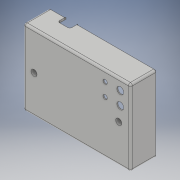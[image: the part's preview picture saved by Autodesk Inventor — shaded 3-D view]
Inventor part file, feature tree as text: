
AUTODESK INVENTOR PART (.ipt)
format: ipt  version: 2019 (Build 230136000, 136)  size: 464,384 bytes
history: native  units: mm
features: other x12, sketch x12, extrude x10, reference x6, fillet x3, projected_geometry x2, shell x1, split x1, hole x1, chamfer x1
ambient origin geometry x8: Origin, YZ Plane, XZ Plane, XY Plane, X Axis, Y Axis, Z Axis, Center Point
bodies: Solid1 (feature_tree)
feature tree (49):
  extrude  "Extrusion1"  Depth=75.0mm
  shell  "Shell1"  Thickness=35.0mm
  fillet  "Fillet2"  Radius=2.0mm
  extrude  "Extrusion10"  Depth=8.0mm
  extrude  "Extrusion11"  Depth=15.0mm
  fillet  "Fillet4"  Radius=15.0mm
  split  "Split1"
  extrude  "Extrusion2"  Depth=5.0mm
  extrude  "Extrusion3"  Depth=3.0mm TaperAngle=0.0deg
  fillet  "Fillet1"  Radius=2.0mm
  other  "Lip1"
  other  "Lip2"
  extrude  "Extrusion4"  Depth=1.0mm
  hole  "Hole1"  [1 undecoded]
  extrude  "Extrusion5"  Depth=8.0mm
  extrude  "Extrusion6"  Depth=23.5mm TaperAngle=0.0deg
  extrude  "Extrusion7"  Depth=5.5mm
  extrude  "Extrusion8"  Depth=3.0mm TaperAngle=0.0deg
  chamfer  "Chamfer1"  Distance=2.0mm
  sketch  "Sketch1"  dims[d0=106.0mm d1=75.0mm d2=35.0mm d3=0.0mm d4=2.0mm]
  sketch  "Sketch2"  dims[d5=9.0mm d6=8.0mm]
  sketch  "Sketch3"  dims[d7=5.0mm d8=0.0mm d9=15.0mm d10=15.0mm]
  reference  "Reference1"
  reference  "Reference2"
  reference  "Reference3"
  reference  "Reference4"
  sketch  "Sketch4"  dims[d11=5.0mm d12=5.0mm]
  projected_geometry  "Projected Loop1"
  sketch  "Sketch5"  dims[d13=4.0mm d14=3.0mm d15=0.0mm d16=2.0mm]
  sketch  "Sketch6"  dims[d17=2.0mm]
  sketch  "Sketch7"  dims[d18=1.0mm d19=1.0mm d20=0.0mm d21=0.0mm d22=0.0mm d23=0.0mm]
  projected_geometry  "Projected Loop2"
  sketch  "Sketch8"  dims[d24=1.0mm d25=1.0mm d26=0.0mm d27=0.0mm d28=0.0mm d29=0.0mm d30=2.6mm]
  sketch  "Sketch9"  dims[d31=2.6mm d32=2.6mm]
  sketch  "Sketch10"  dims[d33=2.6mm d34=8.0mm d35=2.6mm]
  reference  "Reference5"
  reference  "Reference6"
  sketch  "Sketch12"  dims[d36=8.0mm d37=2.6mm]
  sketch  "Sketch13"  dims[d38=3.3mm d39=6.0mm d40=6.0mm d41=21.5mm d42=90.0deg d43=36.25mm d44=0.0mm d45=23.5mm d46=0.0mm d47=5.5mm d48=3.0mm d49=0.0mm d50=2.0mm d51=6.8mm d52=10.0mm d53=10.0mm d54=13.0mm d55=4.3mm d56=15.0mm d57=3.0mm d58=0.0mm d59=11.0mm d60=6.0mm d61=1.0mm d62=0.0mm d63=11.0mm d64=11.0mm d65=30.0mm d66=28.0mm d67=5.1mm d68=0.0mm d69=7.0mm d74=16.0mm d75=12.0mm d76=17.0mm d77=8.0mm d78=10.0mm d79=0.0mm d81=8.0mm d82=17.0mm d83=29.0mm d84=30.0mm d85=10.0mm d86=0.0mm d87=2.0mm d88=8.0mm d89=12.0mm d90=24.375mm d91=18.504mm d92=1.0mm d93=3.5mm d94=2.0mm d95=45.0deg]
  other  "Top"
  other  "Bottom"
  parser-record x1  (decoder bookkeeping rows leaked as tree rows — omitted from the tree; the rows remain in map.json)
  other  "Enclosure Assembly.iam"
  other  "HexaWall-v1.1 v6:1"
  other  "Board:1"
  other  "Packages:1"
  other  "W237-102 (1):X1"
  other  "TB006-508-02P_Green - S:1"
  other  "W237-103:X3"
note: 1 required parameter value undecoded (feature->parameter linkage not recoverable at this tier; creation-order binding heuristic only, values carry confidence <= 0.55)
note: 1 file-system path scrubbed to <path> (originals preserved in map.json)
